# Revit family: Electronics_Commercial-Audio_Biamp_ ThinkSmart_Controller
name_source: partatom
category: Communication Devices
units: mm (PartAtom-declared; Revit-internal decimal feet)

## family parameters
Cut with Voids When Loaded = No
Host = Face
Maintain Annotation Orientation = No
OmniClass Number = 23.85.00.00
OmniClass Title = Information and Communication
Part Type = Normal
Room Calculation Point = No
Round Connector Dimension = Use Diameter
Shared = No

## types (1)
- ThinkSmart Controller
    Connector Description = USB-C 2.0
    Default Elevation = 1219.2 mm  [stored 4 ft]
    Depth = 83.3 mm  [stored 0.273294 ft]
    Description = Lenovo ThinkSmart™ Controller
    Height = 168.1 mm  [stored 0.551509 ft]
    Housing Material = Biamp - Metal - Black
    Manufacturer = Biamp
    Model = ThinkSmart Controller
    Product Documentation Link = https://downloads.biamp.com
    Product Page URL = https://www.biamp.com
    Product data url = https://bimobject.com
    URL = https://www.biamp.com
    Version = 1
    Weight = 0.75 kgf
    Width = 266.5 mm

note: [stored X ft] marks values corroborated as IEEE doubles in the binary element streams (Revit-internal decimal feet)

## geometry (parser evidence)
native form markers: Sweep x5
no freeform markers — native parametric forms only
